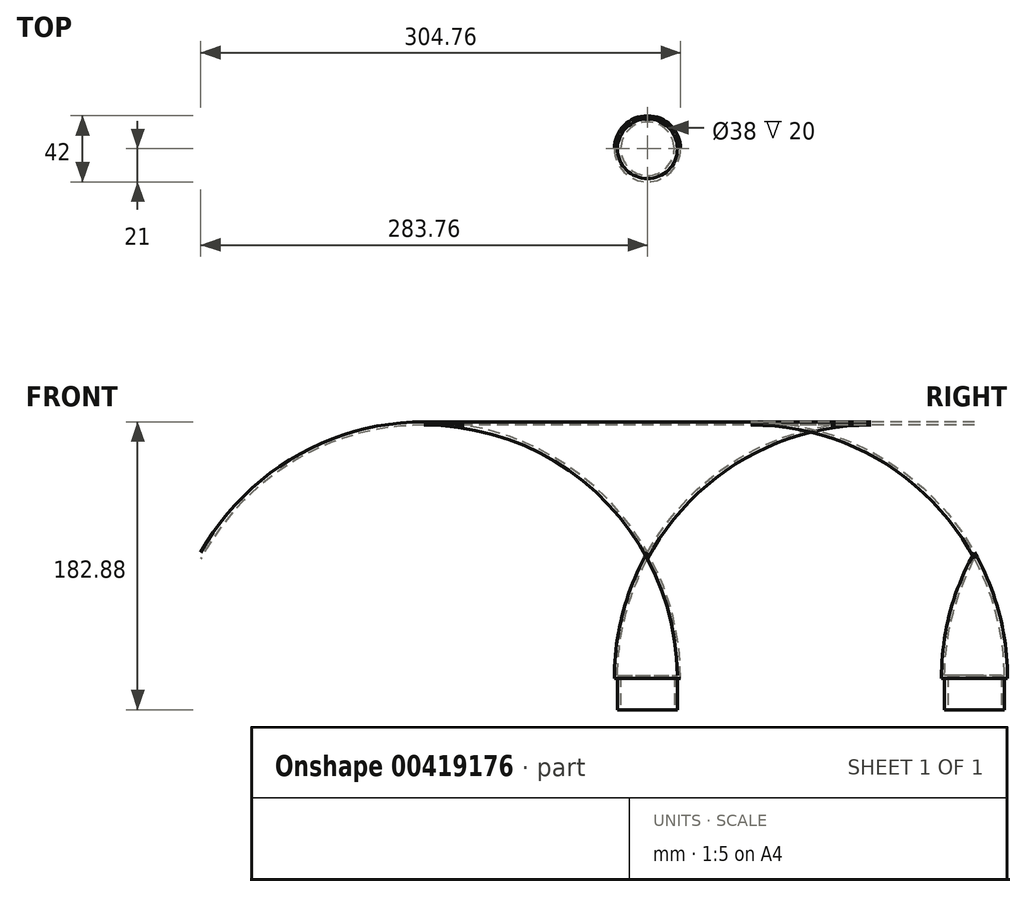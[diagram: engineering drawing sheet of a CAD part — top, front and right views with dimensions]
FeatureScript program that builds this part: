
annotation { "Feature Type Name" : "Feature", "Feature Type Description" : "" }
export const myFeature = defineFeature(function(context is Context, id is Id, definition is map)
    precondition{}
    {
        {
            var Q0;
            Q0=qCreatedBy(makeId("Front.planeOp"),FACE);
            var sketch = newSketch(context, id + "F0", { "sketchPlane" : qUnion([Q0])});
            skLineSegment(sketch, "E0", {"start": v(0, 0) * mm, "end": v(19, 0) * mm});
            skLineSegment(sketch, "E1", {"start": v(19, 0) * mm, "end": v(19, 20) * mm});
            skLineSegment(sketch, "E2", {"start": v(19, 20) * mm, "end": v(21, 20) * mm});
            skLineSegment(sketch, "E3", {"start": v(0, 0) * mm, "end": v(0, 100) * mm});
            skArc(sketch, "E4", {"start": v(21, 20) * mm, "mid": v(15.66, 61.36) * mm, "end": v(0, 100) * mm});
            skArc(sketch, "E5.0", {"start": v(18.99, 22) * mm, "mid": v(13.93, 60.06) * mm, "end": v(0, 95.85) * mm});
            skLineSegment(sketch, "E5.1", {"start": v(17, 22) * mm, "end": v(18.99, 22) * mm});
            skLineSegment(sketch, "E5.2", {"start": v(17, 0) * mm, "end": v(17, 22) * mm});
            skPoint(sketch, "E6.end.orphan", {"position": v(21, 0) * mm});
            skSolve(sketch);
        }
        {
            var Q0;
            {var subQ3=sQuery(id+"F0.wireOp",EDGE,"E1");Q0=makeQuery(id+"F0.imprint","IMPRINT",FACE,{"disambiguationData":[TD([[makeQuery(id+"F0.imprint","IMPRINT",EDGE,{"derivedFrom":subQ3}),1.0]])]});}
            var Q1;
            Q1=sQuery(id+"F0.wireOp",EDGE,"E3");
            revolve(context, id + "F1", {"entities" : qUnion([Q0]), "axis" : qUnion([Q1]), "revolveType" : RevolveType.FULL});
        }
    });
